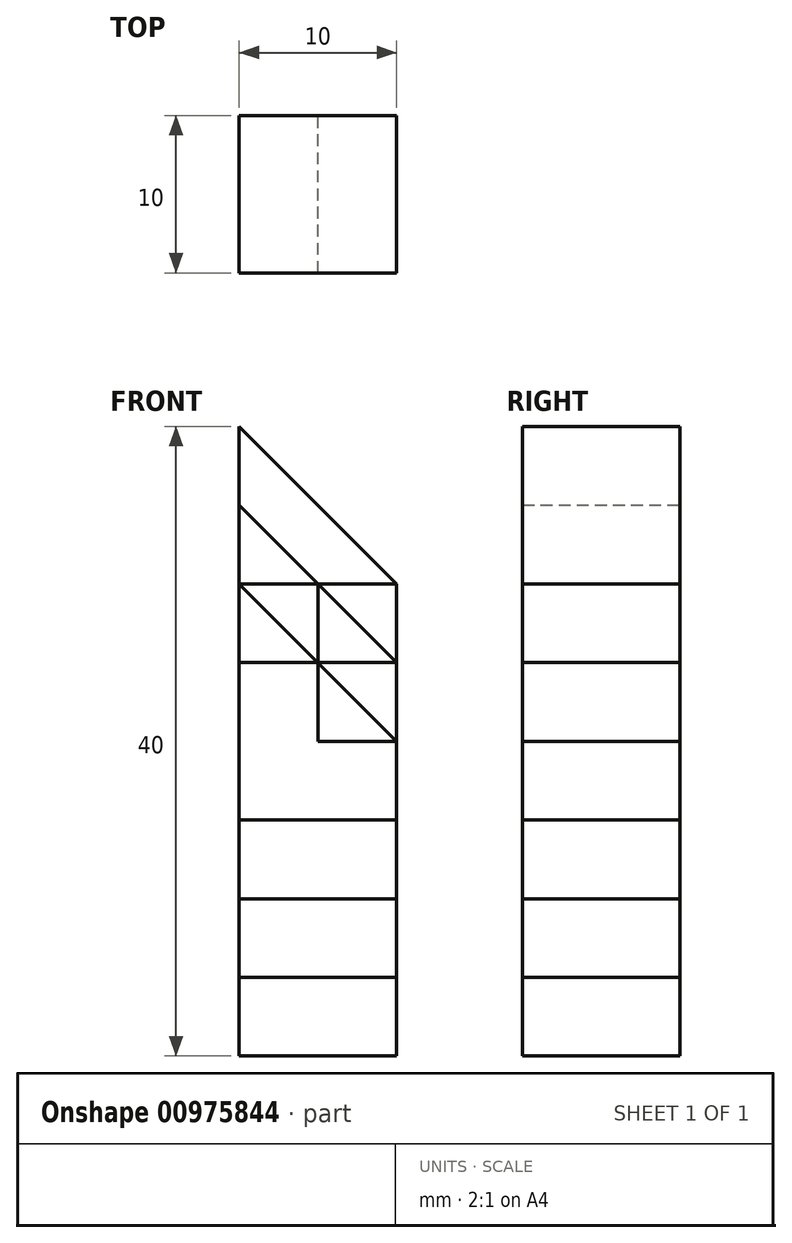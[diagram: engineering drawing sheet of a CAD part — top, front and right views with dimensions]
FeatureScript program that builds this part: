
annotation { "Feature Type Name" : "Feature", "Feature Type Description" : "" }
export const myFeature = defineFeature(function(context is Context, id is Id, definition is map)
    precondition{}
    {
        {
            var Q0;
            Q0=qCreatedBy(makeId("Front.planeOp"),FACE);
            var sketch = newSketch(context, id + "F0", { "sketchPlane" : qUnion([Q0])});
            skLineSegment(sketch, "E0.bottom", {"start": v(-5, 5) * mm, "end": v(5, 5) * mm});
            skLineSegment(sketch, "E0.top", {"start": v(-5, -5) * mm, "end": v(5, -5) * mm});
            skLineSegment(sketch, "E0.left", {"start": v(-5, 5) * mm, "end": v(-5, -5) * mm});
            skLineSegment(sketch, "E0.right", {"start": v(5, 5) * mm, "end": v(5, -5) * mm});
            skPoint(sketch, "E0.middle", {"position": v(0, 0) * mm});
            skSolve(sketch);
        }
        {
            var Q0;
            Q0 = qSketchRegion(id + "F0", true);
            extrude(context, id + "F1", {"entities" : qUnion([Q0]), "endBound" : BoundingType.SYMMETRIC, "depth" : 10 * mm, "offsetDistance" : 25 * mm});
        }
        {
            var Q0;
            Q0=qCreatedBy(makeId("Front.planeOp"),FACE);
            var sketch = newSketch(context, id + "F2", { "sketchPlane" : qUnion([Q0])});
            skLineSegment(sketch, "E1.bottom", {"start": v(-5, 10) * mm, "end": v(5, 10) * mm});
            skLineSegment(sketch, "E1.top", {"start": v(-5, -10) * mm, "end": v(5, -10) * mm});
            skLineSegment(sketch, "E1.left", {"start": v(-5, 10) * mm, "end": v(-5, -10) * mm});
            skLineSegment(sketch, "E1.right", {"start": v(5, 10) * mm, "end": v(5, -10) * mm});
            skPoint(sketch, "E1.middle", {"position": v(0, 0) * mm});
            skSolve(sketch);
        }
        {
            var Q0;
            Q0 = qSketchRegion(id + "F2", true);
            extrude(context, id + "F3", {"entities" : qUnion([Q0]), "endBound" : BoundingType.SYMMETRIC, "depth" : 10 * mm, "offsetDistance" : 25 * mm});
        }
        {
            var Q0;
            Q0=qCreatedBy(makeId("Front.planeOp"),FACE);
            var sketch = newSketch(context, id + "F4", { "sketchPlane" : qUnion([Q0])});
            skLineSegment(sketch, "E2.bottom", {"start": v(-5, 10) * mm, "end": v(0, 10) * mm});
            skLineSegment(sketch, "E2.top", {"start": v(-5, -10) * mm, "end": v(5, -10) * mm});
            skLineSegment(sketch, "E2.left", {"start": v(-5, 10) * mm, "end": v(-5, -10) * mm});
            skLineSegment(sketch, "E2.right", {"start": v(5, 0) * mm, "end": v(5, -10) * mm});
            skPoint(sketch, "E2.middle", {"position": v(0, 0) * mm});
            skLineSegment(sketch, "E3", {"start": v(0, 0) * mm, "end": v(0, 10) * mm});
            skLineSegment(sketch, "E4", {"start": v(0, 0) * mm, "end": v(5, 0) * mm});
            skSolve(sketch);
        }
        {
            var Q0;
            Q0 = qSketchRegion(id + "F4", true);
            extrude(context, id + "F5", {"entities" : qUnion([Q0]), "endBound" : BoundingType.SYMMETRIC, "depth" : 10 * mm, "offsetDistance" : 25 * mm});
        }
        {
            var Q0;
            Q0=qCreatedBy(makeId("Front.planeOp"),FACE);
            var sketch = newSketch(context, id + "F6", { "sketchPlane" : qUnion([Q0])});
            skLineSegment(sketch, "E5.top", {"start": v(5, -10) * mm, "end": v(-5, -10) * mm});
            skLineSegment(sketch, "E5.left", {"start": v(5, 0) * mm, "end": v(5, -10) * mm});
            skLineSegment(sketch, "E5.right", {"start": v(-5, 10) * mm, "end": v(-5, -10) * mm});
            skPoint(sketch, "E5.middle", {"position": v(0, 0) * mm});
            skLineSegment(sketch, "E6", {"start": v(-5, 10) * mm, "end": v(5, 0) * mm});
            skSolve(sketch);
        }
        {
            var Q0;
            Q0 = qSketchRegion(id + "F6", true);
            extrude(context, id + "F7", {"entities" : qUnion([Q0]), "endBound" : BoundingType.SYMMETRIC, "depth" : 10 * mm, "offsetDistance" : 25 * mm});
        }
        {
            var Q0;
            Q0=qCreatedBy(makeId("Front.planeOp"),FACE);
            var sketch = newSketch(context, id + "F8", { "sketchPlane" : qUnion([Q0])});
            skLineSegment(sketch, "E7.top", {"start": v(-5, -15) * mm, "end": v(5, -15) * mm});
            skLineSegment(sketch, "E7.left", {"start": v(-5, 15) * mm, "end": v(-5, -15) * mm});
            skLineSegment(sketch, "E7.right", {"start": v(5, 5) * mm, "end": v(5, -15) * mm});
            skPoint(sketch, "E7.middle", {"position": v(0, 0) * mm});
            skPoint(sketch, "E8", {"position": v(5, 5) * mm});
            skLineSegment(sketch, "E9", {"start": v(-5, 15) * mm, "end": v(5, 5) * mm});
            skSolve(sketch);
        }
        {
            var Q0;
            Q0 = qSketchRegion(id + "F8", true);
            extrude(context, id + "F9", {"entities" : qUnion([Q0]), "endBound" : BoundingType.SYMMETRIC, "depth" : 10 * mm, "offsetDistance" : 25 * mm});
        }
        {
            var Q0;
            Q0=qCreatedBy(makeId("Front.planeOp"),FACE);
            var sketch = newSketch(context, id + "F10", { "sketchPlane" : qUnion([Q0])});
            skLineSegment(sketch, "E10.top", {"start": v(-5, -20) * mm, "end": v(5, -20) * mm});
            skLineSegment(sketch, "E10.left", {"start": v(-5, 20) * mm, "end": v(-5, -20) * mm});
            skLineSegment(sketch, "E10.right", {"start": v(5, 10) * mm, "end": v(5, -20) * mm});
            skPoint(sketch, "E10.middle", {"position": v(0, 0) * mm});
            skPoint(sketch, "E11", {"position": v(5, 10) * mm});
            skLineSegment(sketch, "E12", {"start": v(-5, 20) * mm, "end": v(5, 10) * mm});
            skSolve(sketch);
        }
        {
            var Q0;
            Q0 = qSketchRegion(id + "F10", true);
            extrude(context, id + "F11", {"entities" : qUnion([Q0]), "endBound" : BoundingType.SYMMETRIC, "depth" : 10 * mm, "offsetDistance" : 25 * mm});
        }
    });
